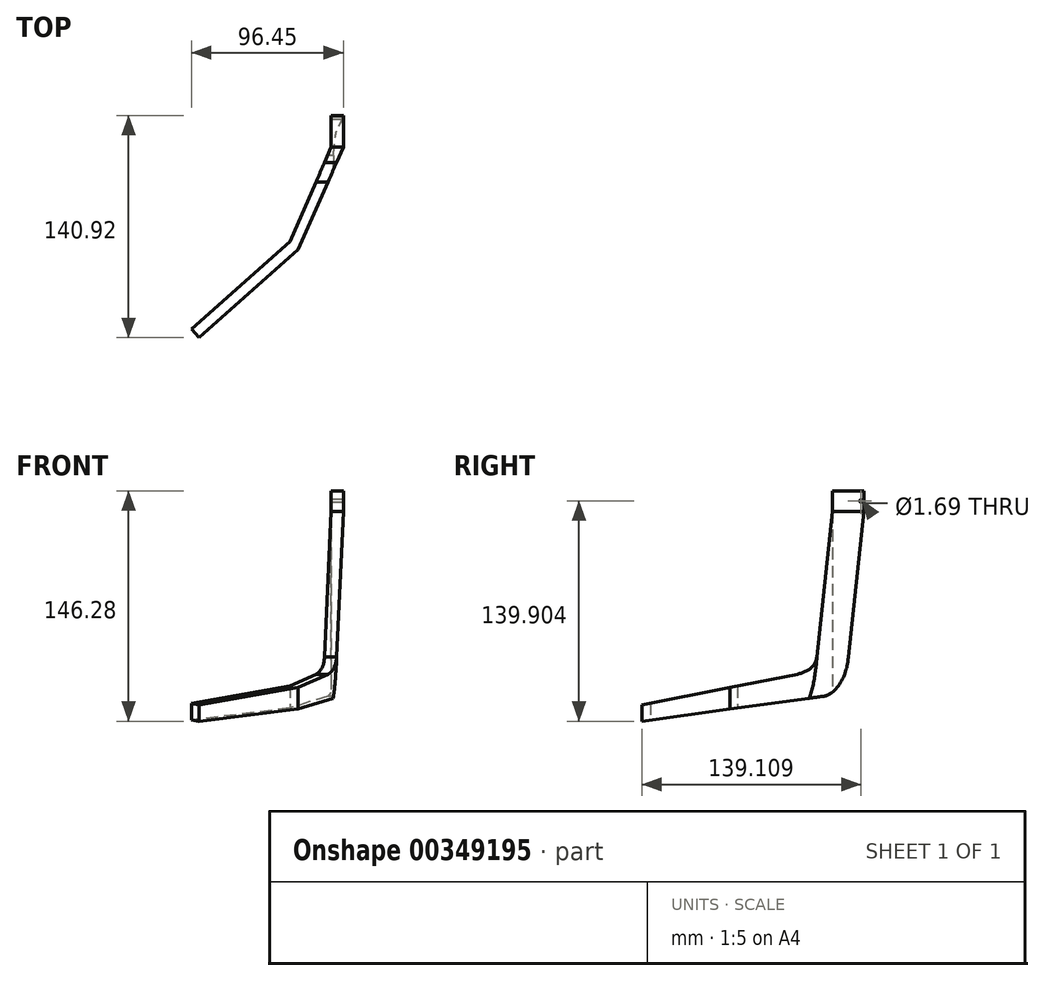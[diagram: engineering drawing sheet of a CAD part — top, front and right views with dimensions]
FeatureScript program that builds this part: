
annotation { "Feature Type Name" : "Feature", "Feature Type Description" : "" }
export const myFeature = defineFeature(function(context is Context, id is Id, definition is map)
    precondition{}
    {
        {
            var Q0;
            Q0=qCreatedBy(makeId("Top.planeOp"),FACE);
            var sketch = newSketch(context, id + "F0", { "sketchPlane" : qUnion([Q0])});
            skLineSegment(sketch, "E0", {"start": v(-5.04, 16.5) * mm, "end": v(-5.04, -16.5) * mm});
            skFitSpline(sketch, "E1", {"points": [v(-5.04, 16.5) * mm, v(5.73, 16.5) * mm], "startDerivative": vector(15.1, 1.4) * mm, "endDerivative": vector(17.18, -1.4) * mm});
            skFitSpline(sketch, "E2.MirrorCS", {"points": [v(-5.04, -16.5) * mm, v(5.73, -16.5) * mm], "startDerivative": vector(15.1, -1.4) * mm, "endDerivative": vector(17.18, 1.4) * mm});
            skArc(sketch, "E3", {"start": v(5.73, -16.5) * mm, "mid": v(7.46, 0) * mm, "end": v(5.73, 16.5) * mm});
            skLineSegment(sketch, "E4.bottom", {"start": v(-8.04, 19.97) * mm, "end": v(18.43, 19.97) * mm});
            skLineSegment(sketch, "E4.top", {"start": v(-8.04, -19.97) * mm, "end": v(18.96, -19.97) * mm});
            skLineSegment(sketch, "E4.left", {"start": v(-8.04, 19.97) * mm, "end": v(-8.04, -19.97) * mm});
            skArc(sketch, "E5", {"start": v(18.96, -19.97) * mm, "mid": v(21, 0.03) * mm, "end": v(18.43, 19.97) * mm});
            skLineSegment(sketch, "E6", {"start": v(-5.54, 17.07) * mm, "end": v(-5.54, -17.07) * mm});
            skArc(sketch, "E7", {"start": v(-5.54, -17.07) * mm, "mid": v(0.38, -17.53) * mm, "end": v(6.29, -17.07) * mm});
            skArc(sketch, "E8.MirrorCS", {"start": v(-5.54, 17.07) * mm, "mid": v(0.38, 17.53) * mm, "end": v(6.29, 17.07) * mm});
            skArc(sketch, "E9", {"start": v(6.29, -17.07) * mm, "mid": v(8.31, 0) * mm, "end": v(6.29, 17.07) * mm});
            skLineSegment(sketch, "E10", {"start": v(-8.04, -9.97) * mm, "end": v(-5.54, -9.97) * mm});
            skLineSegment(sketch, "E11", {"start": v(-8.04, 9.97) * mm, "end": v(-5.54, 9.97) * mm});
            skSolve(sketch);
        }
        {
            var Q0;
            Q0=qCreatedBy(makeId("Front.planeOp"),FACE);
            var sketch = newSketch(context, id + "F1", { "sketchPlane" : qUnion([Q0])});
            skFitSpline(sketch, "E12", {"points": [v(0.57, 7) * mm, v(-1.43, -7) * mm], "startDerivative": vector(-1.3, -21) * mm, "endDerivative": vector(-4.7, -21) * mm});
            skSolve(sketch);
        }
        {
            var Q0;
            Q0=makeQuery(id+"F0.imprint","IMPRINT",FACE,{"disambiguationData":[TD([[makeQuery(id+"F0.imprint","IMPRINT",EDGE,{"derivedFrom":sQuery(id+"F0.wireOp",EDGE,"E0")}),1.0]])]});
            var Q1;
            Q1=sQuery(id+"F1.wireOp",EDGE,"E12");
            sweep(context, id + "F2", {"profiles" : qUnion([Q0]), "path" : qUnion([Q1]), "keepProfileOrientation" : true});
        }
        {
            var Q0;
            Q0=makeQuery(id+"F0.imprint","IMPRINT",FACE,{"disambiguationData":[TD([[makeQuery(id+"F0.imprint","IMPRINT",EDGE,{"derivedFrom":sQuery(id+"F0.wireOp",EDGE,"E4.bottom")}),-1.0]])]});
            var Q1;
            Q1=sQuery(id+"F1.wireOp",EDGE,"E12");
            sweep(context, id + "F3", {"profiles" : qUnion([Q0]), "path" : qUnion([Q1]), "keepProfileOrientation" : true});
        }
        {
            var Q0;
            Q0=qCreatedBy(makeId("Right.planeOp"),FACE);
            var sketch = newSketch(context, id + "F4", { "sketchPlane" : qUnion([Q0])});
            skLineSegment(sketch, "E13.bottom", {"start": v(8.5, -14) * mm, "end": v(-8.5, -14) * mm});
            skLineSegment(sketch, "E13.top", {"start": v(8.5, -7) * mm, "end": v(-8.5, -7) * mm});
            skLineSegment(sketch, "E13.left", {"start": v(8.5, -14) * mm, "end": v(8.5, -7) * mm});
            skLineSegment(sketch, "E13.right", {"start": v(-8.5, -14) * mm, "end": v(-8.5, -7) * mm});
            skSolve(sketch);
        }
        {
            var Q0;
            Q0 = qSketchRegion(id + "F4", true);
            extrude(context, id + "F5", {"entities" : qUnion([Q0]), "operationType" : NewBodyOperationType.REMOVE, "depth" : 13 * mm, "hasSecondDirection" : true, "secondDirectionOppositeDirection" : false, "secondDirectionDepth" : 4.6 * mm});
        }
        {
            var Q0;
            Q0=qCreatedBy(makeId("Right.planeOp"),FACE);
            var sketch = newSketch(context, id + "F6", { "sketchPlane" : qUnion([Q0])});
            skLineSegment(sketch, "E14.bottom", {"start": v(-10, -0.45) * mm, "end": v(10, -0.45) * mm});
            skLineSegment(sketch, "E14.top", {"start": v(-10, -13.45) * mm, "end": v(10, -13.45) * mm});
            skLineSegment(sketch, "E14.left", {"start": v(-10, -0.45) * mm, "end": v(-10, -13.45) * mm});
            skLineSegment(sketch, "E14.right", {"start": v(10, -0.45) * mm, "end": v(10, -13.45) * mm});
            skCircle(sketch, "E15", {"center": v(-8.19, -6.83) * mm, "radius": 0.85 * mm});
            skCircle(sketch, "E16.MirrorC", {"center": v(8.19, -6.83) * mm, "radius": 0.85 * mm});
            skSolve(sketch);
        }
        {
            var Q0;
            Q0=makeQuery(id+"F6.imprint","IMPRINT",FACE,{"disambiguationData":[TD([[makeQuery(id+"F6.imprint","IMPRINT",EDGE,{"derivedFrom":sQuery(id+"F6.wireOp",EDGE,"E15")}),1.0]])]});
            var Q1;
            Q1=makeQuery(id+"F6.imprint","IMPRINT",FACE,{"disambiguationData":[TD([[makeQuery(id+"F6.imprint","IMPRINT",EDGE,{"derivedFrom":sQuery(id+"F6.wireOp",EDGE,"E14.bottom")}),-1.0]])]});
            var Q2;
            Q2=makeQuery(id+"F6.imprint","IMPRINT",FACE,{"disambiguationData":[TD([[makeQuery(id+"F6.imprint","IMPRINT",EDGE,{"derivedFrom":sQuery(id+"F6.wireOp",EDGE,"E16.MirrorC")}),-1.0]])]});
            var Q3;
            Q3=sQuery(id+"F6.wireOp",EDGE,"6pAnekVm-AF5G-etWd-bFE9-uAXiHl3ZONYq");
            extrude(context, id + "F7", {"entities" : qUnion([Q0, Q1, Q2]), "operationType" : NewBodyOperationType.ADD, "surfaceEntities" : qUnion([Q3]), "depth" : 21 * mm, "hasSecondDirection" : true, "secondDirectionOppositeDirection" : false, "secondDirectionDepth" : 13.8 * mm});
        }
        {
            var Q0;
            Q0=makeQuery(id+"F6.imprint","IMPRINT",FACE,{"disambiguationData":[TD([[makeQuery(id+"F6.imprint","IMPRINT",EDGE,{"derivedFrom":sQuery(id+"F6.wireOp",EDGE,"E14.bottom")}),-1.0]])]});
            var Q1;
            Q1=makeQuery(id+"F6.imprint","IMPRINT",FACE,{"disambiguationData":[TD([[makeQuery(id+"F6.imprint","IMPRINT",EDGE,{"derivedFrom":sQuery(id+"F6.wireOp",EDGE,"E15")}),1.0]])]});
            var Q2;
            Q2=makeQuery(id+"F6.imprint","IMPRINT",FACE,{"disambiguationData":[TD([[makeQuery(id+"F6.imprint","IMPRINT",EDGE,{"derivedFrom":sQuery(id+"F6.wireOp",EDGE,"E16.MirrorC")}),-1.0]])]});
            var Q3;
            Q3=sQuery(id+"F6.wireOp",EDGE,"E14.left");
            var Q4;
            Q4=sQuery(id+"F6.wireOp",EDGE,"E14.top");
            var Q5;
            Q5=sQuery(id+"F6.wireOp",EDGE,"E14.right");
            var Q6;
            Q6=sQuery(id+"F6.wireOp",EDGE,"E14.bottom");
            extrude(context, id + "F8", {"entities" : qUnion([Q0, Q1, Q2]), "surfaceEntities" : qUnion([Q3, Q4, Q5, Q6]), "depth" : 30.8 * mm, "hasSecondDirection" : true, "secondDirectionOppositeDirection" : false, "secondDirectionDepth" : 21.06 * mm});
        }
        {
            var Q0;
            Q0=makeQuery(id+"F8.opExtrude","CAP_FACE",FACE,{"disambiguationData":[OSD([sQuery(id+"F6.wireOp",EDGE,"E14.bottom"),sQuery(id+"F6.wireOp",EDGE,"E14.top"),sQuery(id+"F6.wireOp",EDGE,"E14.left"),sQuery(id+"F6.wireOp",EDGE,"E14.right")])],"isStart":false});
            fillet(context, id + "F9", {"entities" : qUnion([Q0]), "radius" : 2 * mm, "tangentPropagation" : true, "allowEdgeOverflow" : false});
        }
        {
            var Q0;
            Q0=makeQuery(id+"F6.imprint","IMPRINT",FACE,{"disambiguationData":[TD([[makeQuery(id+"F6.imprint","IMPRINT",EDGE,{"derivedFrom":sQuery(id+"F6.wireOp",EDGE,"E15")}),1.0]])]});
            var Q1;
            Q1=makeQuery(id+"F6.imprint","IMPRINT",FACE,{"disambiguationData":[TD([[makeQuery(id+"F6.imprint","IMPRINT",EDGE,{"derivedFrom":sQuery(id+"F6.wireOp",EDGE,"E16.MirrorC")}),-1.0]])]});
            var Q2;
            Q2=sQuery(id+"F6.wireOp",EDGE,"E15");
            var Q3;
            Q3=sQuery(id+"F6.wireOp",EDGE,"E16.MirrorC");
            extrude(context, id + "F10", {"entities" : qUnion([Q0, Q1]), "operationType" : NewBodyOperationType.REMOVE, "surfaceEntities" : qUnion([Q2, Q3]), "depth" : 34.2 * mm, "hasSecondDirection" : true, "secondDirectionOppositeDirection" : false, "secondDirectionDepth" : 16.1 * mm});
        }
        {
            var Q0;
            Q0=qCreatedBy(makeId("Right.planeOp"),FACE);
            var sketch = newSketch(context, id + "F11", { "sketchPlane" : qUnion([Q0])});
            skLineSegment(sketch, "E17", {"start": v(10, -13.45) * mm, "end": v(0, -107.63) * mm});
            skLineSegment(sketch, "E18", {"start": v(-10, -13.45) * mm, "end": v(-19.82, -105.94) * mm});
            skLineSegment(sketch, "E19", {"start": v(-32.16, -116.83) * mm, "end": v(-131.17, -136.42) * mm});
            skLineSegment(sketch, "E20", {"start": v(-131.17, -136.42) * mm, "end": v(-131.17, -146.77) * mm});
            skLineSegment(sketch, "E21", {"start": v(-131.17, -146.77) * mm, "end": v(-15.4, -130.8) * mm});
            skFitSpline(sketch, "E22", {"points": [v(0, -107.63) * mm, v(-15.4, -130.8) * mm], "startDerivative": vector(-3.26, -32.34) * mm, "endDerivative": vector(-24.84, -4.35) * mm});
            skFitSpline(sketch, "E23", {"points": [v(-19.82, -105.94) * mm, v(-32.16, -116.83) * mm], "startDerivative": vector(-1.63, -13.6) * mm, "endDerivative": vector(-26.95, -6.67) * mm});
            skLineSegment(sketch, "E24", {"start": v(-10, -13.45) * mm, "end": v(10, -13.45) * mm});
            skSolve(sketch);
        }
        {
            var Q0;
            Q0 = qSketchRegion(id + "F11", true);
            extrude(context, id + "F12", {"entities" : qUnion([Q0]), "operationType" : NewBodyOperationType.ADD, "depth" : 97 * mm, "hasSecondDirection" : true, "secondDirectionOppositeDirection" : true, "secondDirectionDepth" : 132 * mm});
        }
        {
            var Q0;
            Q0=qCreatedBy(makeId("Front.planeOp"),FACE);
            var sketch = newSketch(context, id + "F13", { "sketchPlane" : qUnion([Q0])});
            skLineSegment(sketch, "E25", {"start": v(28.8, -13.45) * mm, "end": v(24.52, -105.94) * mm});
            skLineSegment(sketch, "E26", {"start": v(16.78, -105.94) * mm, "end": v(21.06, -13.45) * mm});
            skLineSegment(sketch, "E27", {"start": v(21.06, -13.45) * mm, "end": v(28.8, -13.45) * mm});
            skLineSegment(sketch, "E28", {"start": v(5.84, -116.83) * mm, "end": v(-109.16, -136.42) * mm});
            skLineSegment(sketch, "E29", {"start": v(-109.16, -136.42) * mm, "end": v(-109.16, -161.29) * mm});
            skLineSegment(sketch, "E30", {"start": v(-109.16, -161.29) * mm, "end": v(18.24, -139.58) * mm});
            skFitSpline(sketch, "E31", {"points": [v(5.84, -116.83) * mm, v(16.78, -105.94) * mm], "startDerivative": vector(23.2, 5.35) * mm, "endDerivative": vector(2.28, 19.17) * mm});
            skFitSpline(sketch, "E32", {"points": [v(18.24, -139.58) * mm, v(24.52, -105.94) * mm], "startDerivative": vector(14.1, 1.94) * mm, "endDerivative": vector(2.48, 49.23) * mm});
            skSolve(sketch);
        }
        {
            var Q0;
            Q0=qCreatedBy(makeId("Top.planeOp"),FACE);
            var sketch = newSketch(context, id + "F14", { "sketchPlane" : qUnion([Q0])});
            skLineSegment(sketch, "E33", {"start": v(21.06, 10) * mm, "end": v(28.8, 10) * mm});
            skLineSegment(sketch, "E34", {"start": v(28.8, 10) * mm, "end": v(28.8, -10) * mm});
            skLineSegment(sketch, "E35", {"start": v(28.8, -10) * mm, "end": v(21.06, -10) * mm});
            skLineSegment(sketch, "E36", {"start": v(21.06, -10) * mm, "end": v(21.06, 10) * mm});
            skLineSegment(sketch, "E37", {"start": v(28.8, -10) * mm, "end": v(0, -74.93) * mm});
            skLineSegment(sketch, "E38", {"start": v(0, -74.93) * mm, "end": v(-62.95, -130.92) * mm});
            skLineSegment(sketch, "E39", {"start": v(-62.95, -130.92) * mm, "end": v(-67.65, -125.64) * mm});
            skLineSegment(sketch, "E40", {"start": v(-67.65, -125.64) * mm, "end": v(-5.2, -70.1) * mm});
            skLineSegment(sketch, "E41", {"start": v(-5.2, -70.1) * mm, "end": v(21.06, -10) * mm});
            skSolve(sketch);
        }
        {
            var Q0;
            Q0 = qSketchRegion(id + "F13", true);
            extrude(context, id + "F15", {"entities" : qUnion([Q0]), "operationType" : NewBodyOperationType.INTERSECT, "depth" : 181 * mm, "hasSecondDirection" : true, "secondDirectionOppositeDirection" : true, "secondDirectionDepth" : 47 * mm});
        }
        {
            var Q0;
            Q0=makeQuery(id+"F14.imprint","IMPRINT",FACE,{"disambiguationData":[TD([[makeQuery(id+"F14.imprint","IMPRINT",EDGE,{"derivedFrom":sQuery(id+"F14.wireOp",EDGE,"E35")}),1.0]])]});
            var Q1;
            Q1=makeQuery(id+"F14.imprint","IMPRINT",FACE,{"disambiguationData":[TD([[makeQuery(id+"F14.imprint","IMPRINT",EDGE,{"derivedFrom":sQuery(id+"F14.wireOp",EDGE,"E33")}),-1.0]])]});
            extrude(context, id + "F16", {"entities" : qUnion([Q0, Q1]), "operationType" : NewBodyOperationType.INTERSECT, "depth" : 71 * mm, "hasSecondDirection" : true, "secondDirectionOppositeDirection" : true, "secondDirectionDepth" : 191 * mm});
        }
        {
            var Q0;
            Q0=makeQuery(id+"F6.imprint","IMPRINT",FACE,{"disambiguationData":[TD([[makeQuery(id+"F6.imprint","IMPRINT",EDGE,{"derivedFrom":sQuery(id+"F6.wireOp",EDGE,"E15")}),1.0]])]});
            var Q1;
            Q1=makeQuery(id+"F6.imprint","IMPRINT",FACE,{"disambiguationData":[TD([[makeQuery(id+"F6.imprint","IMPRINT",EDGE,{"derivedFrom":sQuery(id+"F6.wireOp",EDGE,"E16.MirrorC")}),-1.0]])]});
            var Q2;
            Q2=makeQuery(id+"F6.imprint","IMPRINT",FACE,{"disambiguationData":[TD([[makeQuery(id+"F6.imprint","IMPRINT",EDGE,{"derivedFrom":sQuery(id+"F6.wireOp",EDGE,"E14.bottom")}),-1.0]])]});
            extrude(context, id + "F17", {"entities" : qUnion([Q0, Q1, Q2]), "operationType" : NewBodyOperationType.ADD, "depth" : 28.8 * mm, "hasSecondDirection" : true, "secondDirectionOppositeDirection" : false, "secondDirectionDepth" : 21 * mm});
        }
    });
